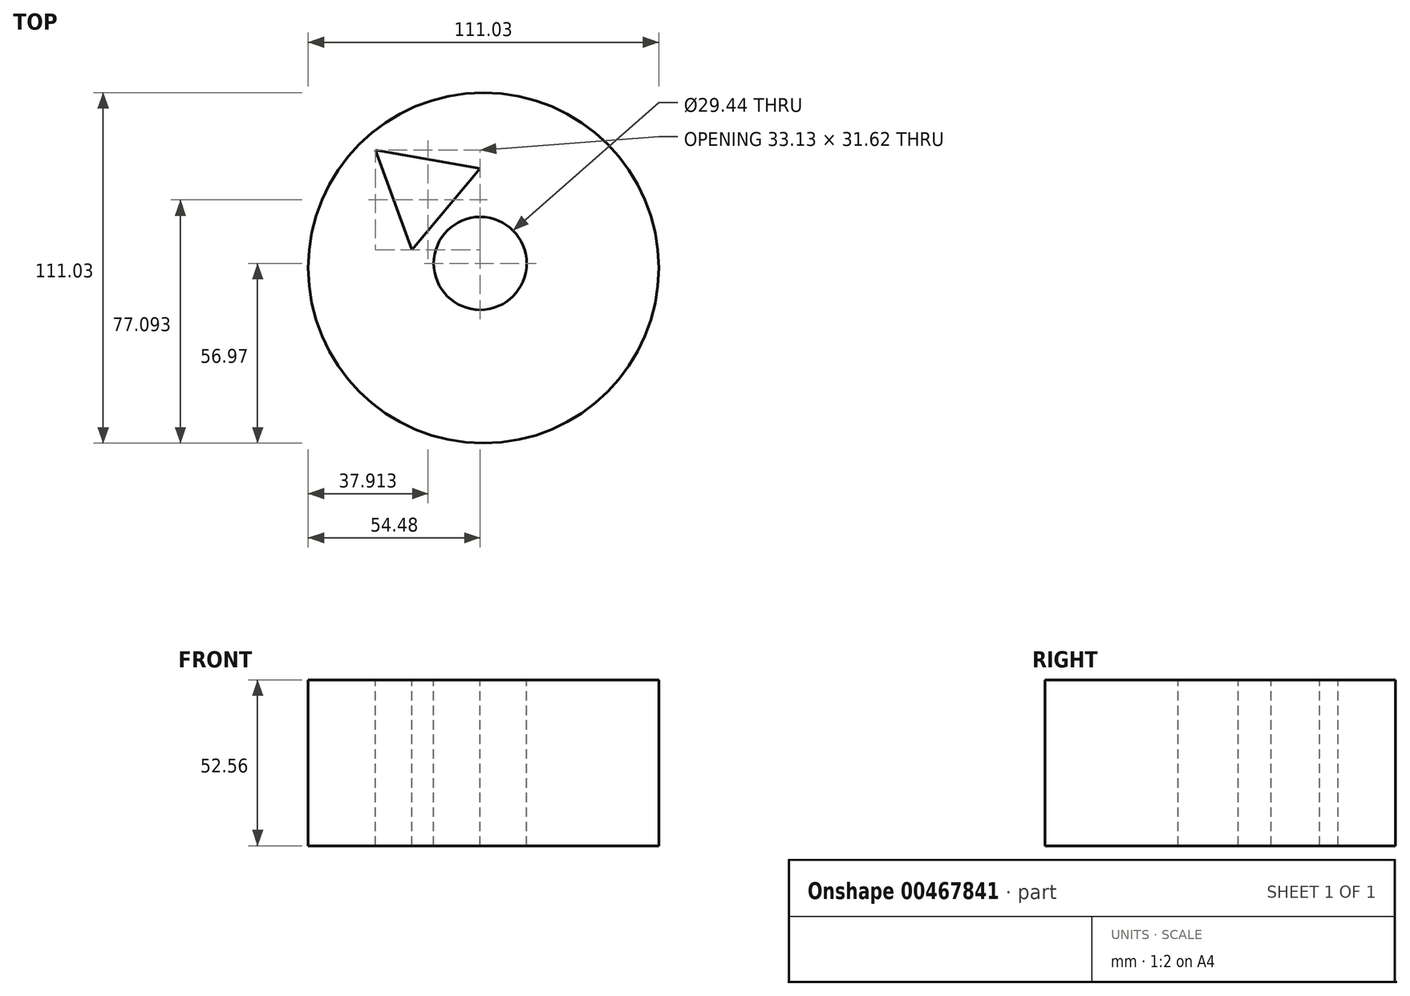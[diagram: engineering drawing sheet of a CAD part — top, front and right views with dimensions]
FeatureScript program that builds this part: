
annotation { "Feature Type Name" : "Feature", "Feature Type Description" : "" }
export const myFeature = defineFeature(function(context is Context, id is Id, definition is map)
    precondition{}
    {
        {
            var Q0;
            Q0=qCreatedBy(makeId("Top.planeOp"),FACE);
            var sketch = newSketch(context, id + "F0", { "sketchPlane" : qUnion([Q0])});
            skCircle(sketch, "E0", {"center": v(1.04, -1.45) * mm, "radius": 55.52 * mm});
            skSolve(sketch);
        }
        {
            var Q0;
            Q0 = qSketchRegion(id + "F0", true);
            extrude(context, id + "F1", {"entities" : qUnion([Q0]), "depth" : 52.55 * mm, "symmetric" : true});
        }
        {
            var Q0;
            Q0=makeQuery(id+"F1.opExtrude","CAP_FACE",FACE,{"disambiguationData":[OSD([sQuery(id+"F0.wireOp",EDGE,"E0")])],"isStart":false});
            var sketch = newSketch(context, id + "F2", { "sketchPlane" : qUnion([Q0])});
            skCircle(sketch, "E1.cCircle", {"center": v(-18.26, 23.44) * mm, "radius": 19.43 * mm, "construction": true});
            skLineSegment(sketch, "E1.0", {"start": v(0, 30.08) * mm, "end": v(-21.64, 4.31) * mm});
            skLineSegment(sketch, "E1.1", {"start": v(-21.64, 4.31) * mm, "end": v(-33.13, 35.93) * mm});
            skLineSegment(sketch, "E1.2", {"start": v(-33.13, 35.93) * mm, "end": v(0, 30.08) * mm});
            skSolve(sketch);
        }
        {
            var Q0;
            Q0 = qSketchRegion(id + "F2", true);
            extrude(context, id + "F3", {"entities" : qUnion([Q0]), "operationType" : NewBodyOperationType.REMOVE, "oppositeDirection" : true, "depth" : 74.13 * mm});
        }
        {
            var Q0;
            Q0=makeQuery(id+"F1.opExtrude","CAP_FACE",FACE,{"disambiguationData":[OSD([sQuery(id+"F0.wireOp",EDGE,"E0")])],"isStart":false});
            var sketch = newSketch(context, id + "F4", { "sketchPlane" : qUnion([Q0])});
            skCircle(sketch, "E2", {"center": v(0, 0) * mm, "radius": 14.72 * mm});
            skSolve(sketch);
        }
        {
            var Q0;
            Q0 = qSketchRegion(id + "F4", true);
            extrude(context, id + "F5", {"entities" : qUnion([Q0]), "operationType" : NewBodyOperationType.REMOVE, "oppositeDirection" : true, "depth" : 121.84 * mm});
        }
    });
